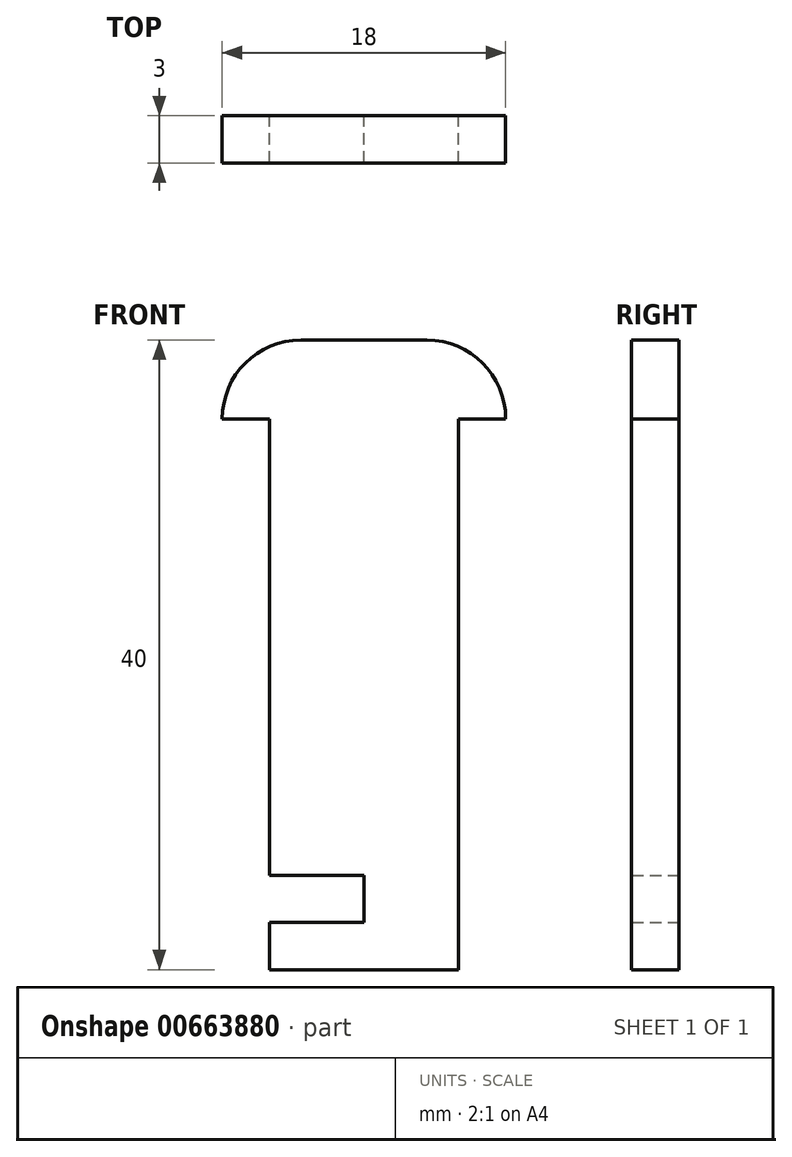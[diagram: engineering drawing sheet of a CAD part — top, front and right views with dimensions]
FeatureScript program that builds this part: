
annotation { "Feature Type Name" : "Feature", "Feature Type Description" : "" }
export const myFeature = defineFeature(function(context is Context, id is Id, definition is map)
    precondition{}
    {
        {
            var Q0;
            Q0=qCreatedBy(makeId("Front.planeOp"),FACE);
            var sketch = newSketch(context, id + "F0", { "sketchPlane" : qUnion([Q0])});
            skLineSegment(sketch, "E0.top", {"start": v(6, -17.5) * mm, "end": v(-6, -17.5) * mm});
            skLineSegment(sketch, "E0.left", {"start": v(6, 17.5) * mm, "end": v(6, -17.5) * mm});
            skLineSegment(sketch, "E0.right", {"start": v(-6, 17.5) * mm, "end": v(-6, -11.5) * mm});
            skPoint(sketch, "E0.middle", {"position": v(0, 0) * mm});
            skLineSegment(sketch, "E1.bottom", {"start": v(9, 17.5) * mm, "end": v(6, 17.5) * mm});
            skLineSegment(sketch, "E1.top", {"start": v(4, 22.5) * mm, "end": v(-4, 22.5) * mm});
            skLineSegment(sketch, "E1.left", {"start": v(9, 17.5) * mm, "end": v(9, 17.5) * mm});
            skLineSegment(sketch, "E1.right", {"start": v(-9, 17.5) * mm, "end": v(-9, 17.5) * mm});
            skLineSegment(sketch, "E2.bottom", {"start": v(-6, -11.5) * mm, "end": v(0, -11.5) * mm});
            skLineSegment(sketch, "E2.top", {"start": v(-6, -14.5) * mm, "end": v(0, -14.5) * mm});
            skLineSegment(sketch, "E2.right", {"start": v(0, -11.5) * mm, "end": v(0, -14.5) * mm});
            skPoint(sketch, "E3.visualSharp", {"position": v(-9, 22.5) * mm});
            skArc(sketch, "E3.filletArc", {"start": v(-4, 22.5) * mm, "mid": v(-7.54, 21.04) * mm, "end": v(-9, 17.5) * mm});
            skPoint(sketch, "E4.visualSharp", {"position": v(9, 22.5) * mm});
            skArc(sketch, "E4.filletArc", {"start": v(9, 17.5) * mm, "mid": v(7.54, 21.04) * mm, "end": v(4, 22.5) * mm});
            skLineSegment(sketch, "E5.trimOffspring", {"start": v(-6, -14.5) * mm, "end": v(-6, -17.5) * mm});
            skLineSegment(sketch, "E6.trimOffspring", {"start": v(-6, 17.5) * mm, "end": v(-9, 17.5) * mm});
            skSolve(sketch);
        }
        {
            var Q0;
            Q0 = qSketchRegion(id + "F0", true);
            extrude(context, id + "F1", {"entities" : qUnion([Q0]), "depth" : 3 * mm, "offsetDistance" : 25 * mm});
        }
    });
